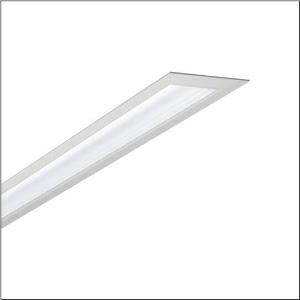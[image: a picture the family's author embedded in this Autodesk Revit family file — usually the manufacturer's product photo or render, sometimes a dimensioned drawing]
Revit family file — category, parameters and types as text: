
# Revit family: silica_r_5mx11bd1w4a_3352
name_source: partatom
category: Lighting Fixtures
units: mm (PartAtom-declared; Revit-internal decimal feet)

## family parameters
Cut with Voids When Loaded = No
Host = Face
Light Source = No
Part Type = Normal
Room Calculation Point = No
Round Connector Dimension = Use Diameter
Shared = No

## types (1)
- --- (1 x LED, 4950 lm, 29.3 W, 4000K)
    Apparent Load = 29 VA
    CIE Flux Codes = 82 97 100 100 100
    Color Rendering = 80
    Color Temperature = 4000K
    Default Elevation = 1800 mm
    Description = Silica®, office luminaire, of aluminium, light emission: direct distribution, primary light characteristic: symmetric, installation type: recessed, LED, rated luminous flux: 4.950lm, luminous efficacy: 169lm/W, light colour: 840, colour temperature: 4000K, control gear: DALI 2, with terminal, 3+2-pole, max. 2.5mm², mains connection: 230V, AC, 50/60Hz, rated input power: 29W, luminaire housing, of aluminium, matt pure white (RAL 9010), length: 1.462mm, width: 93mm, height: 60mm, end cap, of diecast zinc, pure white (RAL 9010), protection rating (complete): IP20, insulation class (complete): insulation class I (protective earthing), certification: CE, permissible operating ambient temperature: 0..+35°C, standard: EN 50419, packaging unit: 1 piece
    Height = 0 mm  [stored 0 ft]
    Lamp = 1 x LED
    Lamp Light Flux = 4950 lm
    Lamp Power = 29.3 W
    Lamp count = 1
    Length = 1462 mm
    Luminous efficacy = 169 lm/W
    Manufacturer = Siteco
    ModVariant = No
    Model = 5MX11BD1W4A
    Mounting Place = Ceiling
    Mounting Type = Recessed
    Number of Poles = 1
    OnlyDefault = Yes
    Power Factor = 1
    Product Name = Silica®
    Product group = office luminaire | ceiling recessed
    ProductGroupID = 401
    Protection Class = Protection class I
    Protection Degree = IP 20
    RLX_Detail_Level = 1
    RLX_Emergency_Light_Flux = 0 lm
    RLX_Emergency_Type = 0
    RLX_Emergency_Type_DB = No
    RlxData = <blob elided: 24029 chars, md5=0ac659dd>
    Socket = socket
    Standby Power = 0 W
    System Light Flux = 4950 lm
    System Power = 29 W
    Type Comments = factory setting: luminous flux: 100 % | dim-lin: 254 | 163 mA
    Type Image = l_1004825.jpg
    URL = http://relux.com
    VarID = @adj_198847
    Voltage = 0 V
    Weight = 0.00 kg
    Width = 93 mm

note: [stored X ft] marks values corroborated as IEEE doubles in the binary element streams (Revit-internal decimal feet)

## geometry (parser evidence)
native form markers: Blend x4, Sweep x10
no freeform markers — native parametric forms only
